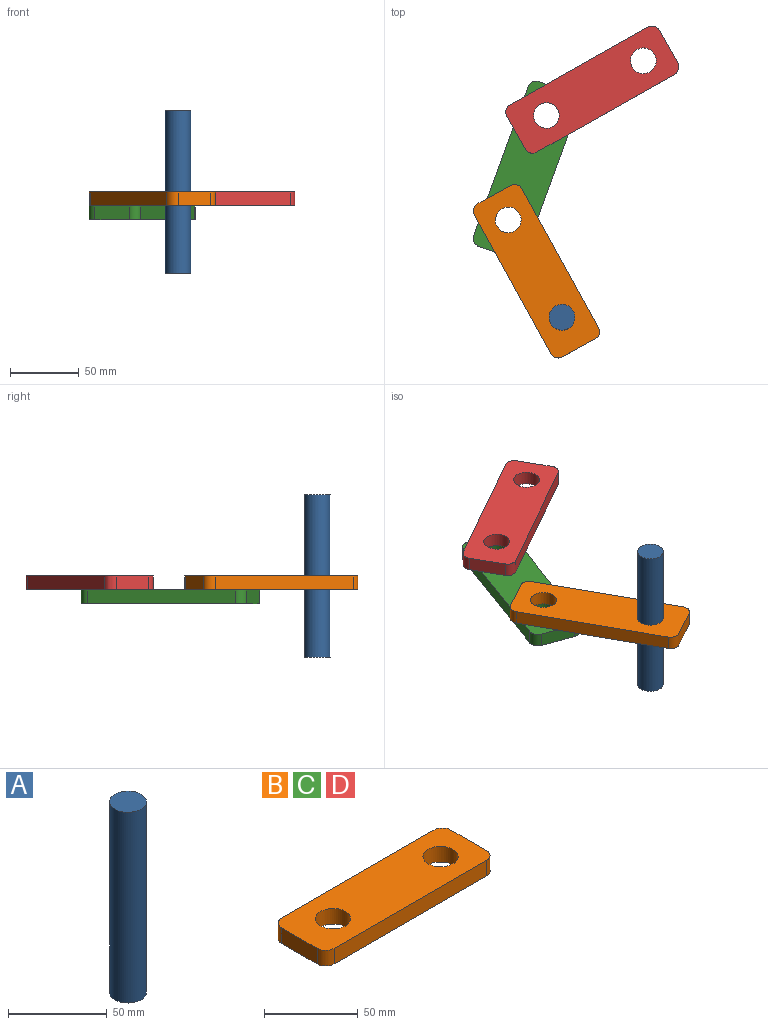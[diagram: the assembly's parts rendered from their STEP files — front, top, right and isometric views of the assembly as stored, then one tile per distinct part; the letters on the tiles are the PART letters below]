
ASSEMBLY  parts=4 mates=3
PART A: 3 faces, bbox 18.7x18.7x118.1 mm
  f0: cylinder r=9.35mm len=118.11mm, axis (0,0,-1), area 6942.2mm2, adj f1,f2
  f1: plane 18.71x18.71mm, normal (0,0,1), area 274.9mm2, adj f0
  f2: plane 18.71x18.71mm, normal (0,0,-1), area 274.9mm2, adj f0
PART B: 12 faces, bbox 127.5x39.6x10.2 mm
  f0: plane 26.86x10.16mm, normal (-1,0,0), area 272.9mm2, adj f1,f9,f10,f11
  f1: cylinder r=6.35mm len=10.16mm, axis (0,0,-1), area 101.3mm2, adj f0,f2,f10,f11
  f2: plane 114.82x10.16mm, normal (0,-1,0), area 1166.5mm2, adj f1,f3,f10,f11
  f3: cylinder r=6.35mm len=10.16mm, axis (0,0,-1), area 101.3mm2, adj f2,f4,f10,f11
  f4: plane 26.86x10.16mm, normal (1,0,0), area 272.9mm2, adj f3,f5,f10,f11
  f5: cylinder r=6.35mm len=10.16mm, axis (0,0,-1), area 101.3mm2, adj f4,f6,f10,f11
  f6: plane 114.82x10.16mm, normal (0,1,0), area 1166.5mm2, adj f5,f9,f10,f11
  f7: cylinder r=9.36mm len=18.72mm, axis (0,0,-1), area 597.4mm2, adj f10,f11
  f8: cylinder r=9.36mm len=18.72mm, axis (0,0,-1), area 597.4mm2, adj f10,f11
  f9: cylinder r=6.35mm len=10.16mm, axis (0,0,-1), area 101.3mm2, adj f0,f6,f10,f11
  f10: plane 127.52x39.56mm, normal (0,0,1), area 4460.1mm2, adj f0,f1,f2,f3,f4,f5,f6,f7
  f11: plane 127.52x39.56mm, normal (0,0,-1), area 4460.1mm2, adj f0,f1,f2,f3,f4,f5,f6,f7
PART C: same geometry as B
PART D: same geometry as B
PLACE A rot(axis=(0.71,0.71,0),180deg) t=(0,0,58.67)mm
PLACE B rot(axis=(0,0,1),118.9deg) t=(-18.53,33.58,48.9)mm
PLACE C rot(axis=(0,0,1),69.9deg) t=(-25.94,106.89,38.74)mm
PLACE D rot(axis=(0,0,1),29.4deg) t=(22.08,165.74,48.9)mm
MATE revolute C.f8 <-> D.f7  axis (0,0,-1) through (-11.32,146.89,48.9)mm
MATE revolute C.f7 <-> B.f8  axis (0,0,-1) through (-39.1,70.87,48.9)mm
MATE revolute A.f0 <-> B.f7  axis (0,0,1) through (0,0,59.06)mm
